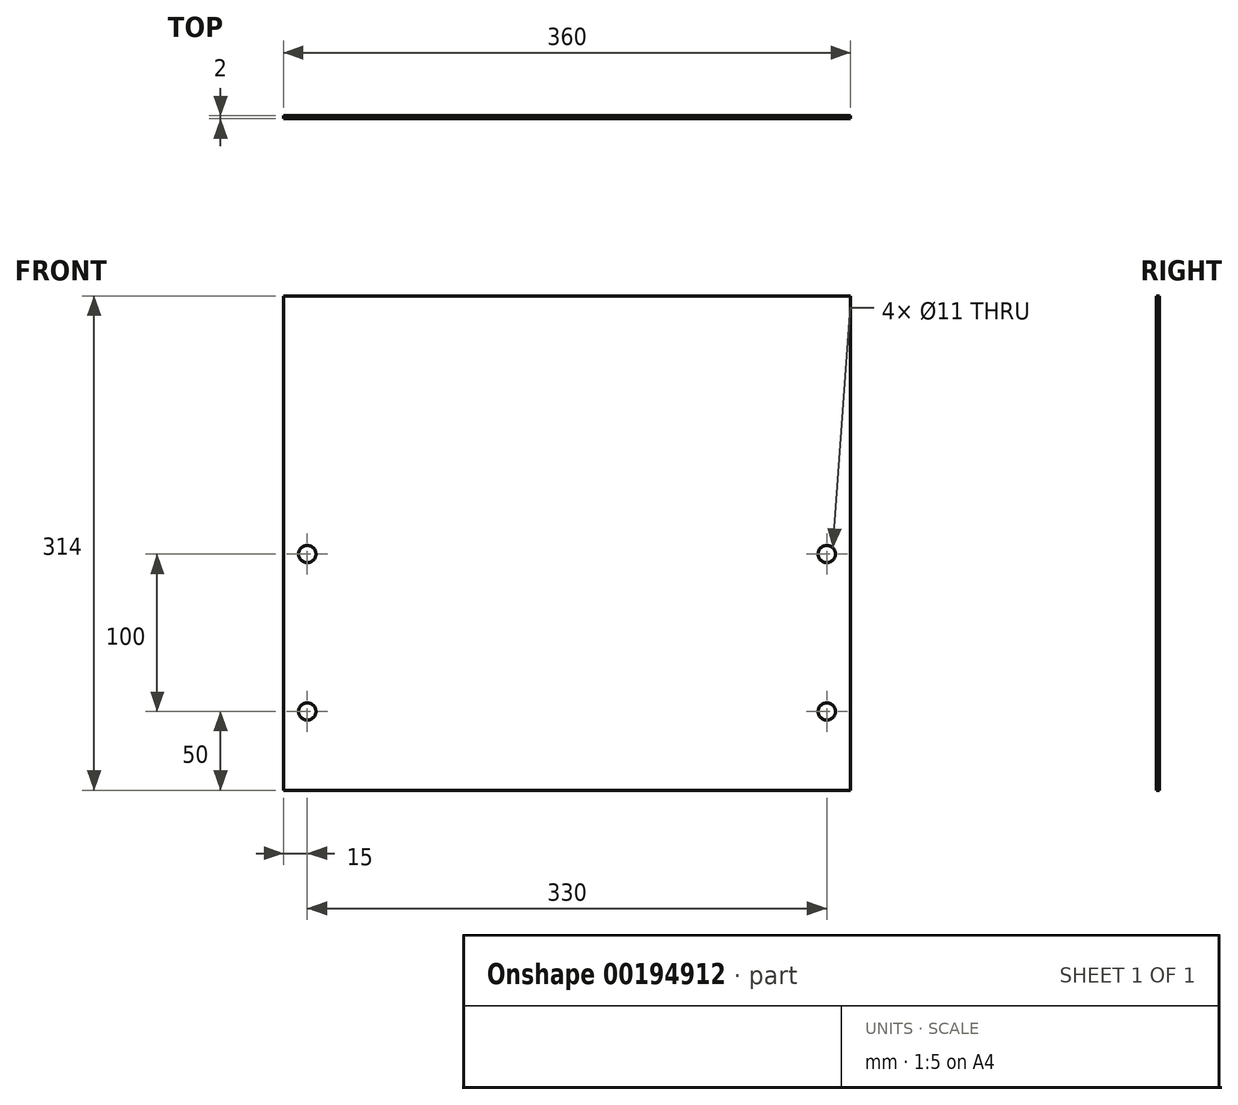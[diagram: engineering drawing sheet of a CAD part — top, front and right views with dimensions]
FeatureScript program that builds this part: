
annotation { "Feature Type Name" : "Feature", "Feature Type Description" : "" }
export const myFeature = defineFeature(function(context is Context, id is Id, definition is map)
    precondition{}
    {
        {
            var Q0;
            Q0=qCreatedBy(makeId("Front.planeOp"),FACE);
            var sketch = newSketch(context, id + "F0", { "sketchPlane" : qUnion([Q0])});
            skLineSegment(sketch, "E0.bottom", {"start": v(0, 0) * mm, "end": v(360, 0) * mm});
            skLineSegment(sketch, "E0.top", {"start": v(0, 314) * mm, "end": v(360, 314) * mm});
            skLineSegment(sketch, "E0.left", {"start": v(0, 0) * mm, "end": v(0, 314) * mm});
            skLineSegment(sketch, "E0.right", {"start": v(360, 0) * mm, "end": v(360, 314) * mm});
            skCircle(sketch, "E1", {"center": v(15, 50) * mm, "radius": 5.5 * mm});
            skCircle(sketch, "E2", {"center": v(15, 150) * mm, "radius": 5.5 * mm});
            skCircle(sketch, "E3", {"center": v(345, 50) * mm, "radius": 5.5 * mm});
            skCircle(sketch, "E4", {"center": v(345, 150) * mm, "radius": 5.5 * mm});
            skSolve(sketch);
        }
        {
            var Q0;
            Q0 = qSketchRegion(id + "F0", true);
            extrude(context, id + "F1", {"entities" : qUnion([Q0]), "depth" : 2 * mm});
        }
    });
